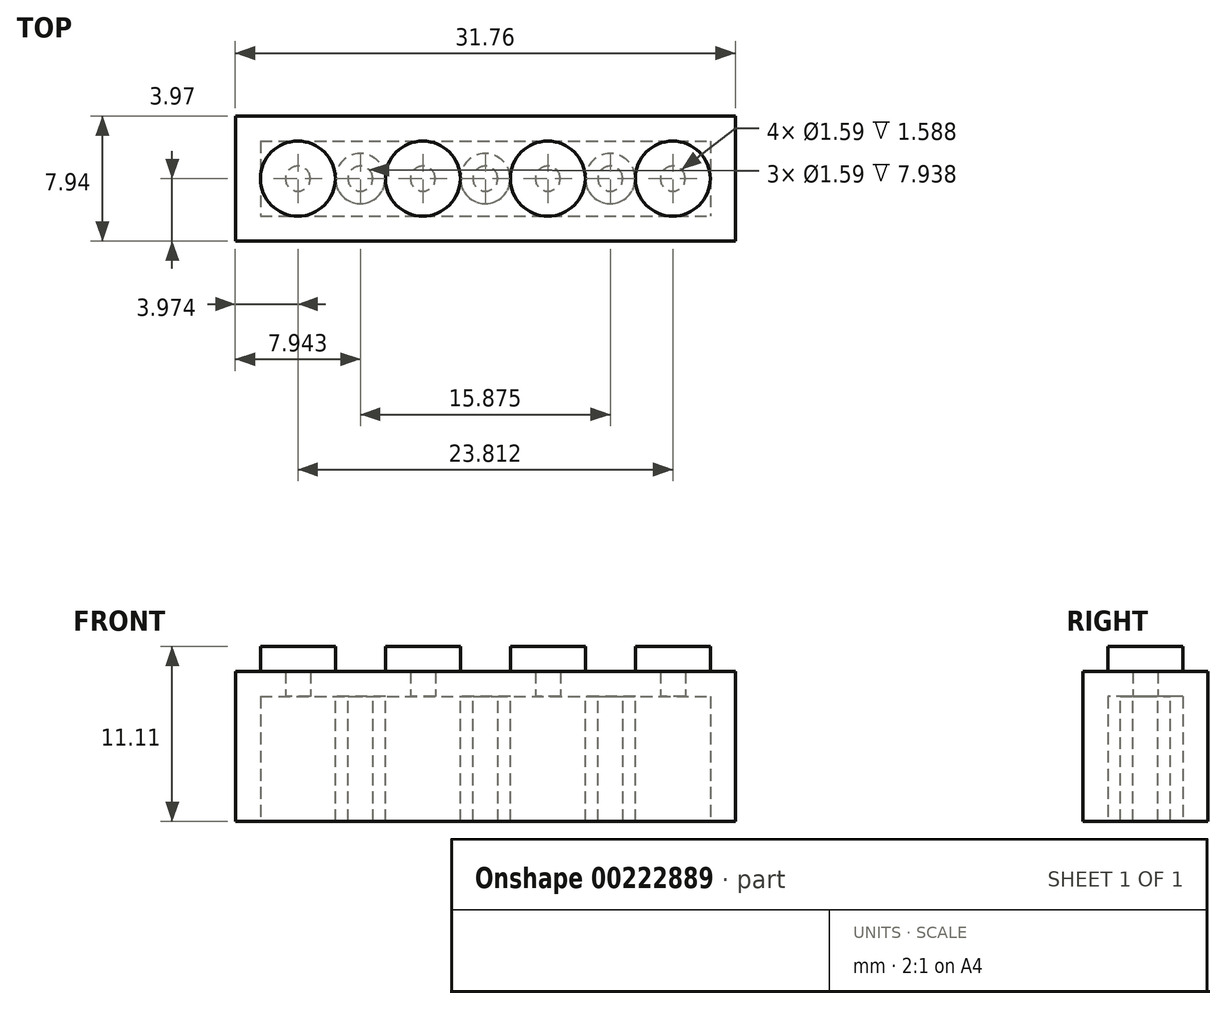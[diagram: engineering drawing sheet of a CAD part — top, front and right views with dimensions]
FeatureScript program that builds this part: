
annotation { "Feature Type Name" : "Feature", "Feature Type Description" : "" }
export const myFeature = defineFeature(function(context is Context, id is Id, definition is map)
    precondition{}
    {
        {
            var Q0;
            Q0=qCreatedBy(makeId("Top.planeOp"),FACE);
            var sketch = newSketch(context, id + "F0", { "sketchPlane" : qUnion([Q0])});
            skLineSegment(sketch, "E0.bottom", {"start": v(-15.88, 3.97) * mm, "end": v(15.88, 3.97) * mm});
            skLineSegment(sketch, "E0.top", {"start": v(-15.88, -3.97) * mm, "end": v(15.88, -3.97) * mm});
            skLineSegment(sketch, "E0.left", {"start": v(-15.88, 3.97) * mm, "end": v(-15.88, -3.97) * mm});
            skLineSegment(sketch, "E0.right", {"start": v(15.88, 3.97) * mm, "end": v(15.88, -3.97) * mm});
            skPoint(sketch, "E0.middle", {"position": v(0, 0) * mm});
            skCircle(sketch, "E1", {"center": v(-11.9, 0) * mm, "radius": 2.38 * mm});
            skCircle(sketch, "E2.1.0.0", {"center": v(-3.97, 0) * mm, "radius": 2.38 * mm});
            skCircle(sketch, "E2.2.0.0", {"center": v(3.97, 0) * mm, "radius": 2.38 * mm});
            skCircle(sketch, "E2.3.0.0", {"center": v(11.9, 0) * mm, "radius": 2.38 * mm});
            skLineSegment(sketch, "E2.direction1", {"start": v(-11.9, 0) * mm, "end": v(-3.97, 0) * mm, "construction": true});
            skSolve(sketch);
        }
        {
            var Q0;
            Q0=makeQuery(id+"F0.imprint","IMPRINT",FACE,{"disambiguationData":[TD([[makeQuery(id+"F0.imprint","IMPRINT",EDGE,{"derivedFrom":sQuery(id+"F0.wireOp",EDGE,"E0.bottom")}),-1.0]])]});
            extrude(context, id + "F1", {"entities" : qUnion([Q0]), "depth" : 9.52 * mm});
        }
        {
            var Q0;
            Q0=makeQuery(id+"F0.imprint","IMPRINT",FACE,{"disambiguationData":[TD([[makeQuery(id+"F0.imprint","IMPRINT",EDGE,{"derivedFrom":sQuery(id+"F0.wireOp",EDGE,"8b71ed98-f0e1-4300-85cb-82ad82c44b3e0.MirrorC")}),-1.0]])]});
            var Q1;
            Q1=makeQuery(id+"F0.imprint","IMPRINT",FACE,{"disambiguationData":[TD([[makeQuery(id+"F0.imprint","IMPRINT",EDGE,{"derivedFrom":sQuery(id+"F0.wireOp",EDGE,"E1")}),1.0]])]});
            var Q2;
            Q2=makeQuery(id+"F0.imprint","IMPRINT",FACE,{"disambiguationData":[TD([[makeQuery(id+"F0.imprint","IMPRINT",EDGE,{"derivedFrom":sQuery(id+"F0.wireOp",EDGE,"E2.1.0.0")}),1.0]])]});
            var Q3;
            Q3=makeQuery(id+"F0.imprint","IMPRINT",FACE,{"disambiguationData":[TD([[makeQuery(id+"F0.imprint","IMPRINT",EDGE,{"derivedFrom":sQuery(id+"F0.wireOp",EDGE,"E2.2.0.0")}),1.0]])]});
            var Q4;
            Q4=makeQuery(id+"F0.imprint","IMPRINT",FACE,{"disambiguationData":[TD([[makeQuery(id+"F0.imprint","IMPRINT",EDGE,{"derivedFrom":sQuery(id+"F0.wireOp",EDGE,"E2.3.0.0")}),1.0]])]});
            extrude(context, id + "F2", {"entities" : qUnion([Q0, Q1, Q2, Q3, Q4]), "operationType" : NewBodyOperationType.ADD, "depth" : 11.1 * mm});
        }
        {
            var Q0;
            {var subQ0=sQuery(id+"F0.wireOp",EDGE,"8b71ed98-f0e1-4300-85cb-82ad82c44b3e0.MirrorC");var subQ1=sQuery(id+"F0.wireOp",EDGE,"E1");Q0=makeQuery(id+"F2.boolean.opBoolean","MERGE",FACE,{"derivedFrom":[makeQuery(id+"F1.opExtrude","CAP_FACE",FACE,{"disambiguationData":[OSD([sQuery(id+"F0.wireOp",EDGE,"E0.bottom"),sQuery(id+"F0.wireOp",EDGE,"E0.top"),sQuery(id+"F0.wireOp",EDGE,"E0.left"),sQuery(id+"F0.wireOp",EDGE,"E0.right"),subQ1,subQ0])],"isStart":true}),makeQuery(id+"F2.opExtrude","CAP_FACE",FACE,{"disambiguationData":[OSD([subQ1])],"isStart":true}),makeQuery(id+"F2.opExtrude","CAP_FACE",FACE,{"disambiguationData":[OSD([subQ0])],"isStart":true})]});}
            shell(context, id + "F3", {"entities" : qUnion([Q0]), "thickness" : 1.59 * mm});
        }
        {
            var Q0;
            Q0=makeQuery(id+"F3.opShell","OFFSET_FACE",FACE,{"disambiguationData":[OSD([sQuery(id+"F0.wireOp",EDGE,"E0.bottom"),sQuery(id+"F0.wireOp",EDGE,"E0.top"),sQuery(id+"F0.wireOp",EDGE,"E0.left"),sQuery(id+"F0.wireOp",EDGE,"E0.right"),sQuery(id+"F0.wireOp",EDGE,"E1"),sQuery(id+"F0.wireOp",EDGE,"8b71ed98-f0e1-4300-85cb-82ad82c44b3e0.MirrorC")])]});
            var sketch = newSketch(context, id + "F4", { "sketchPlane" : qUnion([Q0])});
            skCircle(sketch, "E3", {"center": v(-7.94, 0) * mm, "radius": 1.59 * mm});
            skCircle(sketch, "E4", {"center": v(-7.94, 0) * mm, "radius": 0.8 * mm});
            skCircle(sketch, "E5.1.0.0", {"center": v(0, 0) * mm, "radius": 1.59 * mm});
            skCircle(sketch, "E5.1.0.1", {"center": v(0, 0) * mm, "radius": 0.8 * mm});
            skCircle(sketch, "E5.2.0.0", {"center": v(7.94, 0) * mm, "radius": 1.59 * mm});
            skCircle(sketch, "E5.2.0.1", {"center": v(7.94, 0) * mm, "radius": 0.8 * mm});
            skLineSegment(sketch, "E5.direction1", {"start": v(-7.94, 0) * mm, "end": v(0, 0) * mm, "construction": true});
            skSolve(sketch);
        }
        {
            var Q0;
            Q0=makeQuery(id+"F4.imprint","IMPRINT",FACE,{"disambiguationData":[TD([[makeQuery(id+"F4.imprint","IMPRINT",EDGE,{"derivedFrom":sQuery(id+"F4.wireOp",EDGE,"E3")}),1.0]])]});
            var Q1;
            Q1=makeQuery(id+"F4.imprint","IMPRINT",FACE,{"disambiguationData":[TD([[makeQuery(id+"F4.imprint","IMPRINT",EDGE,{"derivedFrom":sQuery(id+"F4.wireOp",EDGE,"E5.1.0.0")}),1.0]])]});
            var Q2;
            Q2=makeQuery(id+"F4.imprint","IMPRINT",FACE,{"disambiguationData":[TD([[makeQuery(id+"F4.imprint","IMPRINT",EDGE,{"derivedFrom":sQuery(id+"F4.wireOp",EDGE,"E5.2.0.0")}),1.0]])]});
            extrude(context, id + "F5", {"entities" : qUnion([Q0, Q1, Q2]), "operationType" : NewBodyOperationType.ADD, "depth" : 7.94 * mm});
        }
    });
